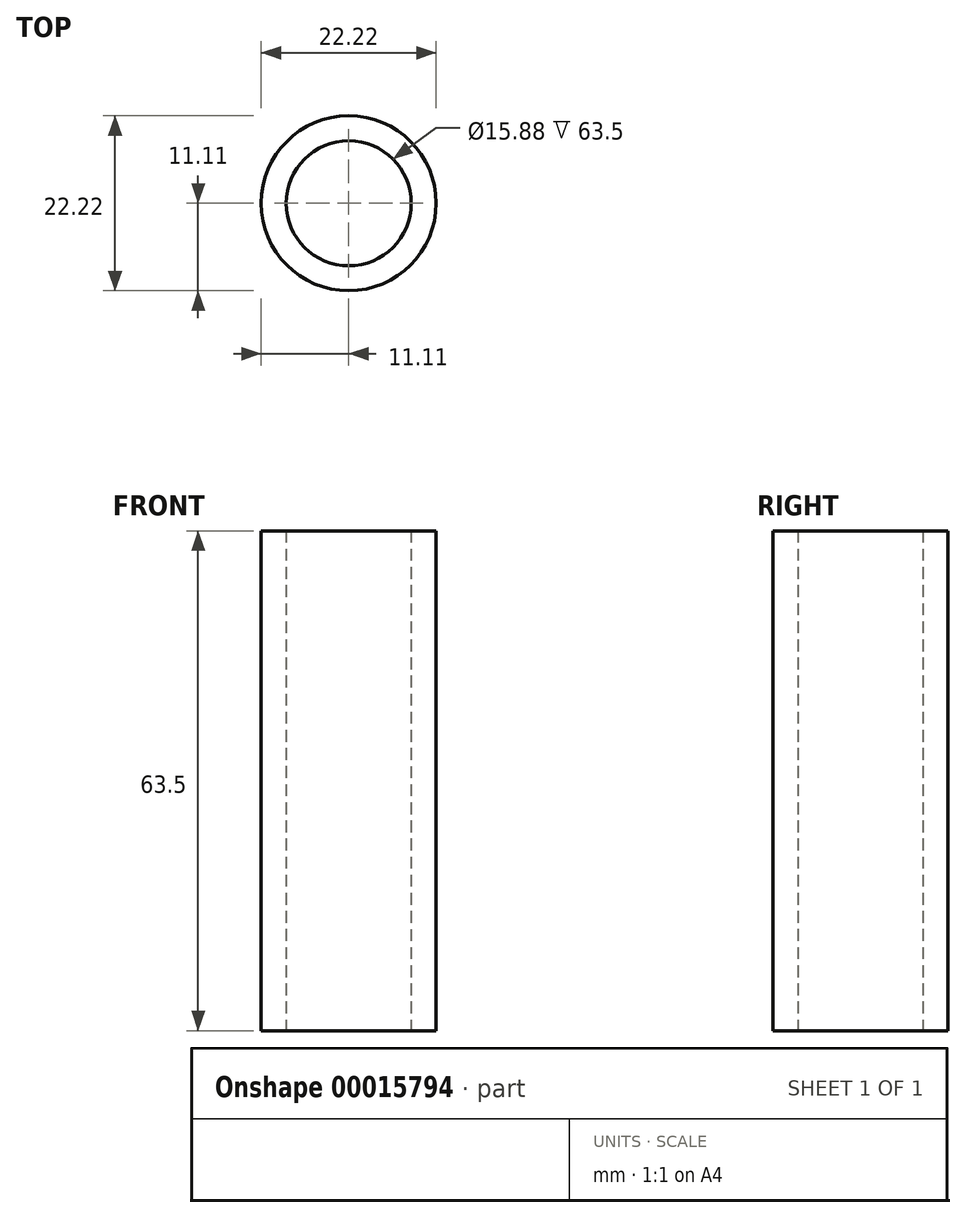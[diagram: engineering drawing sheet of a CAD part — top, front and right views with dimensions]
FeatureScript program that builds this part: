
annotation { "Feature Type Name" : "Feature", "Feature Type Description" : "" }
export const myFeature = defineFeature(function(context is Context, id is Id, definition is map)
    precondition{}
    {
        {
            var Q0;
            Q0=qCreatedBy(makeId("Top.planeOp"),FACE);
            var sketch = newSketch(context, id + "F0", { "sketchPlane" : qUnion([Q0])});
            skCircle(sketch, "E0", {"center": v(0, 0) * mm, "radius": 11.11 * mm});
            skCircle(sketch, "E1", {"center": v(0, 0) * mm, "radius": 7.94 * mm});
            skSolve(sketch);
        }
        {
            var Q0;
            Q0=qSketchRegion(id+"F0",true);
            extrude(context, id + "F1", {"entities" : qUnion([Q0]), "depth" : 63.5 * mm});
        }
    });
